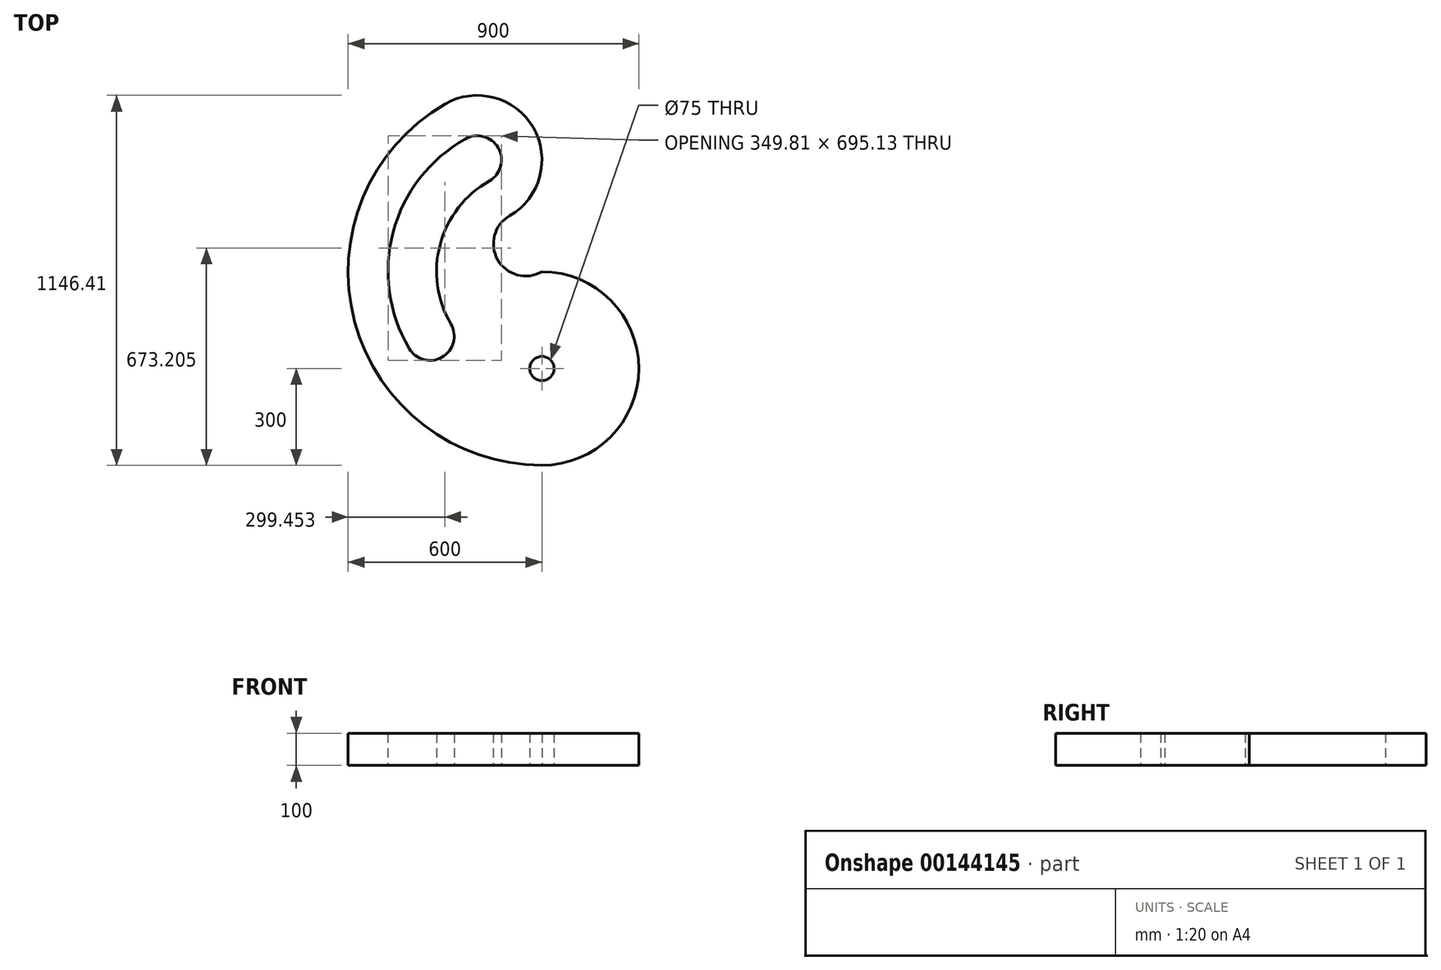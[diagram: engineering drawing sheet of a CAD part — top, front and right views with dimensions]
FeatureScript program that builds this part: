
annotation { "Feature Type Name" : "Feature", "Feature Type Description" : "" }
export const myFeature = defineFeature(function(context is Context, id is Id, definition is map)
    precondition{}
    {
        {
            var Q0;
            Q0=qCreatedBy(makeId("Top.planeOp"),FACE);
            var sketch = newSketch(context, id + "F0", { "sketchPlane" : qUnion([Q0])});
            skArc(sketch, "E0", {"start": v(0, -600) * mm, "mid": v(300, -300) * mm, "end": v(0, 0) * mm});
            skArc(sketch, "E1", {"start": v(-100, 173.2) * mm, "mid": v(-136.6, 36.6) * mm, "end": v(0, 0) * mm});
            skArc(sketch, "E2", {"start": v(-100, 173.2) * mm, "mid": v(-26.8, 446.41) * mm, "end": v(-300, 519.62) * mm});
            skArc(sketch, "E3", {"start": v(-300, 519.62) * mm, "mid": v(-579.56, -155.3) * mm, "end": v(0, -600) * mm});
            skCircle(sketch, "E4", {"center": v(0, -300) * mm, "radius": 37.5 * mm});
            skArc(sketch, "E5", {"start": v(-237.5, 411.36) * mm, "mid": v(-135.05, 383.91) * mm, "end": v(-162.5, 281.46) * mm});
            skArc(sketch, "E6", {"start": v(-281.46, -162.5) * mm, "mid": v(-308.91, -264.95) * mm, "end": v(-411.36, -237.5) * mm});
            skArc(sketch, "E7", {"start": v(-237.5, 411.36) * mm, "mid": v(-460.34, 123.35) * mm, "end": v(-411.36, -237.5) * mm});
            skArc(sketch, "E8", {"start": v(-162.5, 281.46) * mm, "mid": v(-315.13, 84.44) * mm, "end": v(-281.46, -162.5) * mm});
            skSolve(sketch);
        }
        {
            var Q0;
            Q0=makeQuery(id+"F0.imprint","IMPRINT",FACE,{"disambiguationData":[TD([[makeQuery(id+"F0.imprint","IMPRINT",EDGE,{"derivedFrom":sQuery(id+"F0.wireOp",EDGE,"E0")}),1.0]])]});
            extrude(context, id + "F1", {"entities" : qUnion([Q0]), "depth" : 100 * mm});
        }
    });
